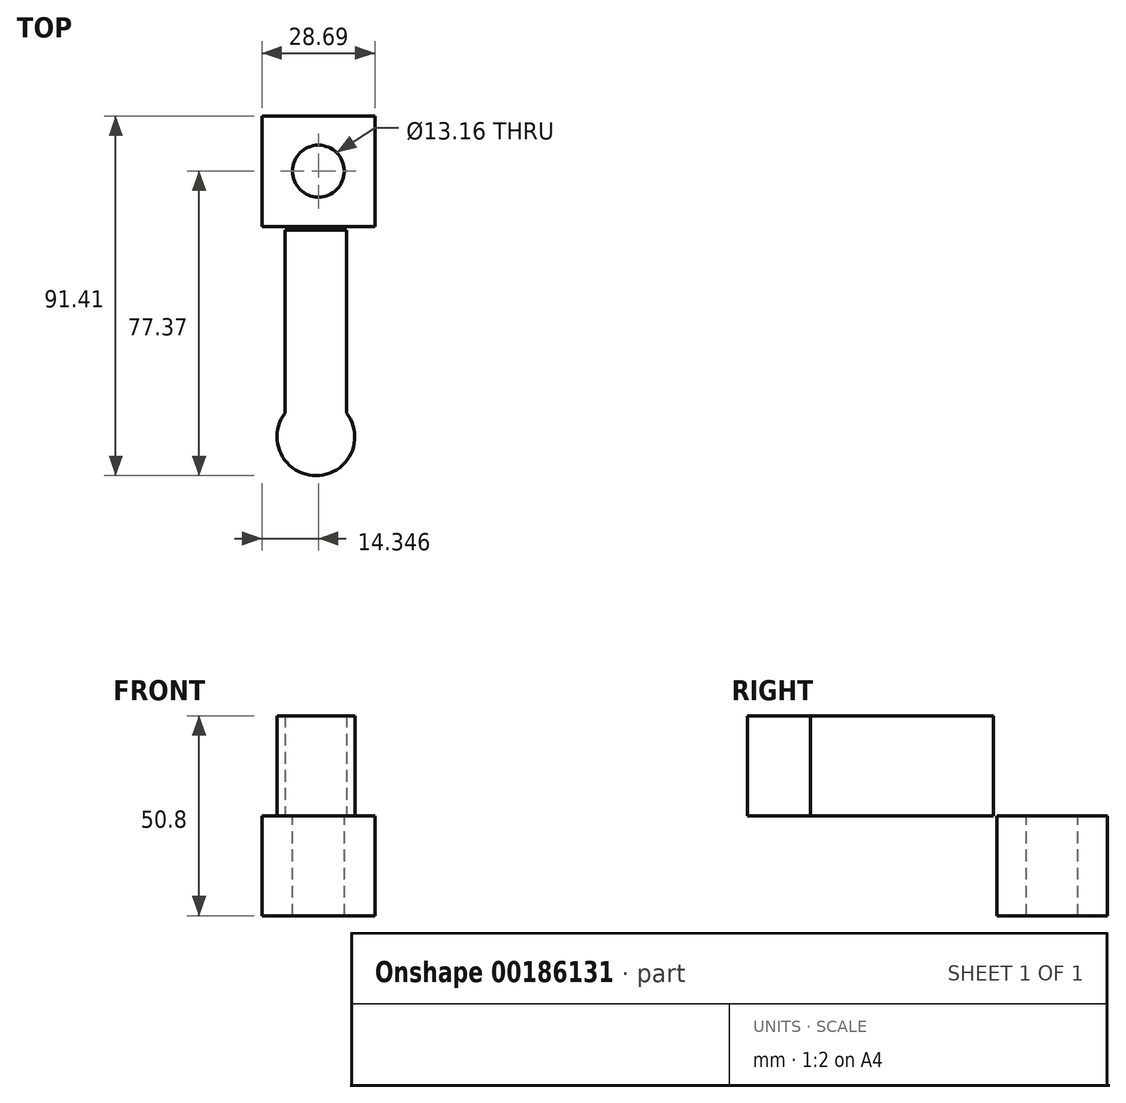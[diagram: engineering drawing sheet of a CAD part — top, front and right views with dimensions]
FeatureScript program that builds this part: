
annotation { "Feature Type Name" : "Feature", "Feature Type Description" : "" }
export const myFeature = defineFeature(function(context is Context, id is Id, definition is map)
    precondition{}
    {
        {
            var Q0;
            Q0=qCreatedBy(makeId("Top.planeOp"),FACE);
            var sketch = newSketch(context, id + "F0", { "sketchPlane" : qUnion([Q0])});
            skLineSegment(sketch, "E0.bottom", {"start": v(-50.53, 48.82) * mm, "end": v(-21.84, 48.82) * mm});
            skLineSegment(sketch, "E0.top", {"start": v(-50.53, 20.74) * mm, "end": v(-21.84, 20.74) * mm});
            skLineSegment(sketch, "E0.left", {"start": v(-50.53, 48.82) * mm, "end": v(-50.53, 20.74) * mm});
            skLineSegment(sketch, "E0.right", {"start": v(-21.84, 48.82) * mm, "end": v(-21.84, 20.74) * mm});
            skSolve(sketch);
        }
        {
            var Q0;
            Q0=makeQuery(id+"F0.imprint","IMPRINT",FACE,{"disambiguationData":[TD([[makeQuery(id+"F0.imprint","IMPRINT",EDGE,{"derivedFrom":sQuery(id+"F0.wireOp",EDGE,"E0.bottom")}),-1.0]])]});
            extrude(context, id + "F1", {"entities" : qUnion([Q0]), "depth" : 25.4 * mm});
        }
        {
            var Q0;
            Q0=makeQuery(id+"F1.opExtrude","CAP_FACE",FACE,{"disambiguationData":[OSD([sQuery(id+"F0.wireOp",EDGE,"E0.bottom"),sQuery(id+"F0.wireOp",EDGE,"E0.top"),sQuery(id+"F0.wireOp",EDGE,"E0.left"),sQuery(id+"F0.wireOp",EDGE,"E0.right")])],"isStart":false});
            var sketch = newSketch(context, id + "F2", { "sketchPlane" : qUnion([Q0])});
            skCircle(sketch, "E1", {"center": v(-36.18, 34.78) * mm, "radius": 6.58 * mm});
            skSolve(sketch);
        }
        {
            var Q0;
            Q0=makeQuery(id+"F2.imprint","IMPRINT",FACE,{"disambiguationData":[TD([[makeQuery(id+"F2.imprint","IMPRINT",EDGE,{"derivedFrom":sQuery(id+"F2.wireOp",EDGE,"E1")}),1.0]])]});
            extrude(context, id + "F3", {"entities" : qUnion([Q0]), "operationType" : NewBodyOperationType.REMOVE, "endBound" : BoundingType.UP_TO_NEXT, "oppositeDirection" : true, "depth" : 25.4 * mm});
        }
        {
            var Q0;
            Q0=qCreatedBy(makeId("Top.planeOp"),FACE);
            cPlane(context, id + "F4", {"entities" : qUnion([Q0]), "cplaneType" : CPlaneType.OFFSET, "offset" : 25.4 * mm, "width" : 152.4 * mm, "height" : 152.4 * mm});
        }
        {
            var Q0;
            Q0=qCreatedBy(id+"F4.planeOp",FACE);
            var sketch = newSketch(context, id + "F5", { "sketchPlane" : qUnion([Q0])});
            skLineSegment(sketch, "E2.bottom", {"start": v(-44.6, 19.8) * mm, "end": v(-29, 19.8) * mm});
            skLineSegment(sketch, "E2.top", {"start": v(-44.6, -26.67) * mm, "end": v(-29, -26.67) * mm});
            skLineSegment(sketch, "E2.left", {"start": v(-44.6, 19.8) * mm, "end": v(-44.6, -26.67) * mm});
            skLineSegment(sketch, "E2.right", {"start": v(-29, 19.8) * mm, "end": v(-29, -26.67) * mm});
            skArc(sketch, "E3", {"start": v(-44.6, -26.67) * mm, "mid": v(-36.8, -42.59) * mm, "end": v(-29, -26.67) * mm});
            skSolve(sketch);
        }
        {
            var Q0;
            Q0=makeQuery(id+"F5.imprint","IMPRINT",FACE,{"disambiguationData":[TD([[makeQuery(id+"F5.imprint","IMPRINT",EDGE,{"derivedFrom":sQuery(id+"F5.wireOp",EDGE,"E2.bottom")}),-1.0]])]});
            var Q1;
            Q1=makeQuery(id+"F5.imprint","IMPRINT",FACE,{"disambiguationData":[TD([[makeQuery(id+"F5.imprint","IMPRINT",EDGE,{"derivedFrom":sQuery(id+"F5.wireOp",EDGE,"E2.top")}),-1.0]])]});
            extrude(context, id + "F6", {"entities" : qUnion([Q0, Q1]), "depth" : 25.4 * mm});
        }
    });
